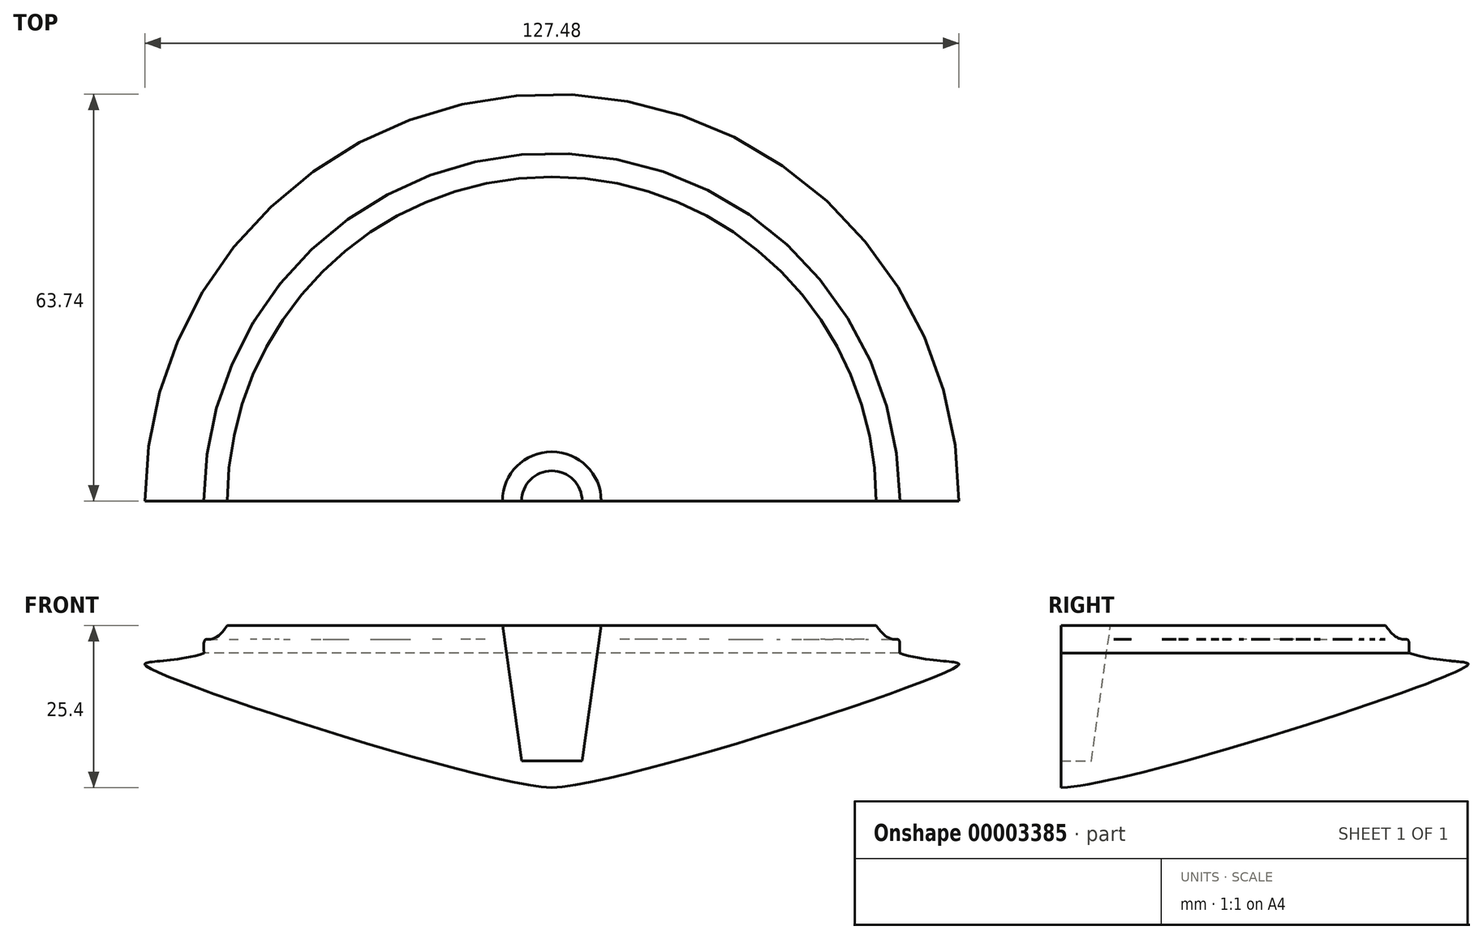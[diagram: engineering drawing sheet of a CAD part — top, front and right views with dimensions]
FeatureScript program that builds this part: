
annotation { "Feature Type Name" : "Feature", "Feature Type Description" : "" }
export const myFeature = defineFeature(function(context is Context, id is Id, definition is map)
    precondition{}
    {
        {
            var Q0;
            Q0=qCreatedBy(makeId("Front.planeOp"),FACE);
            var sketch = newSketch(context, id + "F0", { "sketchPlane" : qUnion([Q0])});
            skFitSpline(sketch, "E0", {"points": [v(-50.8, 0) * mm, v(-54.44, -4.34) * mm], "startDerivative": vector(-8.88, -13.02) * mm, "endDerivative": vector(0.84, -13.02) * mm});
            skFitSpline(sketch, "E1", {"points": [v(-54.44, -4.34) * mm, v(-63.5, -6.35) * mm, v(0, -25.4) * mm], "startDerivative": vector(-60.9, -19.04) * mm, "endDerivative": vector(45.9, -1.7) * mm});
            skLineSegment(sketch, "E2", {"start": v(-50.8, 0) * mm, "end": v(0, 0) * mm});
            skLineSegment(sketch, "E3", {"start": v(0, 0) * mm, "end": v(0, -25.4) * mm});
            skLineSegment(sketch, "E4", {"start": v(-63.5, -25.4) * mm, "end": v(0, -25.4) * mm});
            skLineSegment(sketch, "E5", {"start": v(-63.5, -6.35) * mm, "end": v(-63.5, -25.4) * mm});
            skLineSegment(sketch, "E6", {"start": v(-14, -0.88) * mm, "end": v(-52.76, -6.35) * mm});
            skLineSegment(sketch, "E7", {"start": v(-52.76, -6.35) * mm, "end": v(-5.06, -21.18) * mm});
            skLineSegment(sketch, "E8", {"start": v(-5.06, -21.18) * mm, "end": v(-14, -0.88) * mm});
            skLineSegment(sketch, "E9", {"start": v(-7.73, 0) * mm, "end": v(-4.74, -21.18) * mm});
            skLineSegment(sketch, "E10", {"start": v(-4.74, -21.18) * mm, "end": v(0, -21.18) * mm});
            skSolve(sketch);
        }
        {
            var Q0;
            {var subQ6=sQuery(id+"F0.wireOp",EDGE,"E0");Q0=makeQuery(id+"F0.imprint","IMPRINT",FACE,{"disambiguationData":[TD([[makeQuery(id+"F0.imprint","IMPRINT",EDGE,{"derivedFrom":subQ6}),1.0]])]});}
            var Q1;
            Q1=makeQuery(id+"F0.imprint","IMPRINT",FACE,{"disambiguationData":[TD([[makeQuery(id+"F0.imprint","IMPRINT",EDGE,{"derivedFrom":sQuery(id+"F0.wireOp",EDGE,"E6")}),1.0]])]});
            var Q2;
            Q2=sQuery(id+"F0.wireOp",EDGE,"E3");
            revolve(context, id + "F1", {"entities" : qUnion([Q0, Q1]), "axis" : qUnion([Q2]), "revolveType" : RevolveType.ONE_DIRECTION, "angle" : 180 * degree});
        }
        {
            var Q0;
            Q0=qCreatedBy(makeId("Front.planeOp"),FACE);
            cPlane(context, id + "F2", {"entities" : qUnion([Q0]), "cplaneType" : CPlaneType.OFFSET, "offset" : 54.6 * mm, "width" : 152.4 * mm, "height" : 152.4 * mm});
        }
        {
            var Q0;
            Q0=qCreatedBy(id+"F2.planeOp",FACE);
            var sketch = newSketch(context, id + "F3", { "sketchPlane" : qUnion([Q0])});
            skFitSpline(sketch, "E11", {"points": [v(-4.22, -2.76) * mm, v(-2.96, -2.69) * mm, v(-3.42, -3.1) * mm, v(-3.72, -3.85) * mm, v(-3.84, -3.14) * mm, v(-4.22, -2.76) * mm]});
            skFitSpline(sketch, "E12", {"points": [v(-2.72, -2.76) * mm, v(-2.8, -3.77) * mm, v(-2.35, -3.4) * mm, v(-2.13, -3.85) * mm, v(-1.98, -2.76) * mm, v(-2.35, -3.1) * mm, v(-2.72, -2.76) * mm]});
            skFitSpline(sketch, "E13", {"points": [v(-0.9, -2.83) * mm, v(-1.5, -2.85) * mm, v(-1.51, -3.72) * mm, v(-0.9, -3.72) * mm, v(-1.3, -3.52) * mm, v(-0.93, -3.38) * mm, v(-1.26, -3.22) * mm, v(-0.9, -2.83) * mm]});
            skFitSpline(sketch, "E14", {"points": [v(-0.3, -2.87) * mm, v(-0.3, -3.85) * mm, v(0.09, -3.35) * mm, v(0.47, -3.12) * mm, v(0.16, -2.73) * mm, v(-0.3, -2.87) * mm]});
            skFitSpline(sketch, "E15", {"points": [v(-0.09, -2.87) * mm, v(-0.1, -3.28) * mm, v(0.09, -3.09) * mm, v(-0.09, -2.87) * mm]});
            skFitSpline(sketch, "E16", {"points": [v(1.37, -2.72) * mm, v(0.8, -3.25) * mm, v(1.07, -3.73) * mm, v(1.7, -3.41) * mm, v(1.75, -3.12) * mm, v(1.37, -2.72) * mm]});
            skFitSpline(sketch, "E17", {"points": [v(1.32, -3.04) * mm, v(1.15, -3.32) * mm, v(1.44, -3.38) * mm, v(1.32, -3.04) * mm]});
            skFitSpline(sketch, "E18", {"points": [v(2.38, -2.8) * mm, v(1.93, -3.72) * mm, v(2.73, -3.63) * mm, v(2.32, -3.51) * mm, v(2.38, -2.8) * mm]});
            skFitSpline(sketch, "E19", {"points": [v(3.41, -2.92) * mm, v(3.12, -3.65) * mm, v(3.51, -3.3) * mm, v(3.41, -2.92) * mm]});
            skFitSpline(sketch, "E20", {"points": [v(4.35, -2.92) * mm, v(3.9, -3.16) * mm, v(3.88, -3.57) * mm, v(4.35, -3.67) * mm, v(4.2, -3.4) * mm, v(4.35, -2.92) * mm]});
            skFitSpline(sketch, "E21", {"points": [v(5.37, -2.92) * mm, v(4.76, -2.91) * mm, v(4.76, -3.62) * mm, v(5.35, -3.69) * mm, v(5.07, -3.48) * mm, v(5.34, -3.38) * mm, v(4.93, -3.16) * mm, v(5.37, -2.92) * mm]});
            skSolve(sketch);
        }
        {
            var Q0;
            Q0=makeQuery(id+"F3.imprint","IMPRINT",FACE,{"disambiguationData":[TD([[makeQuery(id+"F3.imprint","IMPRINT",EDGE,{"derivedFrom":sQuery(id+"F3.wireOp",EDGE,"E12")}),1.0]])]});
            var Q1;
            Q1=makeQuery(id+"F3.imprint","IMPRINT",FACE,{"disambiguationData":[TD([[makeQuery(id+"F3.imprint","IMPRINT",EDGE,{"derivedFrom":sQuery(id+"F3.wireOp",EDGE,"E13")}),1.0]])]});
            var Q2;
            Q2=makeQuery(id+"F3.imprint","IMPRINT",FACE,{"disambiguationData":[TD([[makeQuery(id+"F3.imprint","IMPRINT",EDGE,{"derivedFrom":sQuery(id+"F3.wireOp",EDGE,"E18")}),1.0]])]});
            var Q3;
            Q3=makeQuery(id+"F3.imprint","IMPRINT",FACE,{"disambiguationData":[TD([[makeQuery(id+"F3.imprint","IMPRINT",EDGE,{"derivedFrom":sQuery(id+"F3.wireOp",EDGE,"E19")}),1.0]])]});
            var Q4;
            Q4=makeQuery(id+"F3.imprint","IMPRINT",FACE,{"disambiguationData":[TD([[makeQuery(id+"F3.imprint","IMPRINT",EDGE,{"derivedFrom":sQuery(id+"F3.wireOp",EDGE,"E20")}),1.0]])]});
            var Q5;
            Q5=makeQuery(id+"F3.imprint","IMPRINT",FACE,{"disambiguationData":[TD([[makeQuery(id+"F3.imprint","IMPRINT",EDGE,{"derivedFrom":sQuery(id+"F3.wireOp",EDGE,"E21")}),1.0]])]});
            var Q6;
            Q6=makeQuery(id+"F3.imprint","IMPRINT",FACE,{"disambiguationData":[TD([[makeQuery(id+"F3.imprint","IMPRINT",EDGE,{"derivedFrom":sQuery(id+"F3.wireOp",EDGE,"E14")}),1.0]])]});
            var Q7;
            Q7=makeQuery(id+"F3.imprint","IMPRINT",FACE,{"disambiguationData":[TD([[makeQuery(id+"F3.imprint","IMPRINT",EDGE,{"derivedFrom":sQuery(id+"F3.wireOp",EDGE,"E16")}),1.0]])]});
            var Q8;
            Q8=makeQuery(id+"F3.imprint","IMPRINT",FACE,{"disambiguationData":[TD([[makeQuery(id+"F3.imprint","IMPRINT",EDGE,{"derivedFrom":sQuery(id+"F3.wireOp",EDGE,"E11")}),-1.0]])]});
            extrude(context, id + "F4", {"entities" : qUnion([Q0, Q1, Q2, Q3, Q4, Q5, Q6, Q7, Q8]), "operationType" : NewBodyOperationType.REMOVE, "oppositeDirection" : true, "depth" : 0.4 * mm});
        }
        {
            var Q0;
            Q0=qCreatedBy(makeId("Top.planeOp"),FACE);
            cPlane(context, id + "F5", {"entities" : qUnion([Q0]), "cplaneType" : CPlaneType.OFFSET, "offset" : 4.32 * mm, "oppositeDirection" : true, "width" : 152.4 * mm, "height" : 152.4 * mm});
        }
        {
            var Q0;
            Q0=qCreatedBy(id+"F5.planeOp",FACE);
            var sketch = newSketch(context, id + "F6", { "sketchPlane" : qUnion([Q0])});
            skFitSpline(sketch, "E22", {"points": [v(-6.97, -57.02) * mm, v(-7.1, -61.02) * mm, v(-5.4, -58.81) * mm, v(-2.83, -57.39) * mm, v(-6.97, -57.02) * mm]});
            skFitSpline(sketch, "E23", {"points": [v(-5.36, -57.48) * mm, v(-6.6, -58.35) * mm, v(-5.04, -57.85) * mm, v(-5.36, -57.48) * mm]});
            skFitSpline(sketch, "E24", {"points": [v(0.71, -57.85) * mm, v(-2.46, -59.32) * mm, v(0, -61.66) * mm, v(2.78, -59.83) * mm, v(0.71, -57.85) * mm]});
            skFitSpline(sketch, "E25", {"points": [v(0, -59.18) * mm, v(0, -60.8) * mm, v(1.5, -60.06) * mm, v(0, -59.18) * mm]});
            skFitSpline(sketch, "E26", {"points": [v(4.66, -58.08) * mm, v(4.48, -61.34) * mm, v(7.7, -59.87) * mm, v(5.22, -60.1) * mm, v(4.66, -58.08) * mm]});
            skFitSpline(sketch, "E27", {"points": [v(8.85, -57.53) * mm, v(9.4, -60.33) * mm, v(10.64, -58.45) * mm, v(8.85, -57.53) * mm]});
            skFitSpline(sketch, "E28", {"points": [v(14, -56.24) * mm, v(12.02, -58.86) * mm, v(16.76, -60) * mm, v(14.1, -58.5) * mm, v(14, -56.24) * mm]});
            skFitSpline(sketch, "E29", {"points": [v(18.5, -54.9) * mm, v(16.3, -55.82) * mm, v(18.23, -59) * mm, v(20.53, -57.53) * mm, v(17.95, -57.66) * mm, v(19.15, -56.24) * mm, v(17.13, -56.65) * mm, v(18.5, -54.9) * mm]});
            skSolve(sketch);
        }
        {
            var Q0;
            {Q0=qUnion([makeQuery(id+"F6.imprint","IMPRINT",FACE,{"disambiguationData":[TD([[makeQuery(id+"F6.imprint","IMPRINT",EDGE,{"derivedFrom":sQuery(id+"F6.wireOp",EDGE,"E26")}),1.0]])]}),makeQuery(id+"F6.imprint","IMPRINT",FACE,{"disambiguationData":[TD([[makeQuery(id+"F6.imprint","IMPRINT",EDGE,{"derivedFrom":sQuery(id+"F6.wireOp",EDGE,"E27")}),1.0]])]}),makeQuery(id+"F6.imprint","IMPRINT",FACE,{"disambiguationData":[TD([[makeQuery(id+"F6.imprint","IMPRINT",EDGE,{"derivedFrom":sQuery(id+"F6.wireOp",EDGE,"E28")}),1.0]])]}),makeQuery(id+"F6.imprint","IMPRINT",FACE,{"disambiguationData":[TD([[makeQuery(id+"F6.imprint","IMPRINT",EDGE,{"derivedFrom":sQuery(id+"F6.wireOp",EDGE,"E29")}),1.0]])]}),makeQuery(id+"F6.imprint","IMPRINT",FACE,{"disambiguationData":[TD([[makeQuery(id+"F6.imprint","IMPRINT",EDGE,{"derivedFrom":sQuery(id+"F6.wireOp",EDGE,"E22")}),1.0]])]}),makeQuery(id+"F6.imprint","IMPRINT",FACE,{"disambiguationData":[TD([[makeQuery(id+"F6.imprint","IMPRINT",EDGE,{"derivedFrom":sQuery(id+"F6.wireOp",EDGE,"E24")}),1.0]])]})]);}
            extrude(context, id + "F7", {"entities" : qUnion([Q0]), "operationType" : NewBodyOperationType.REMOVE, "oppositeDirection" : true, "depth" : 1.27 * mm});
        }
    });
